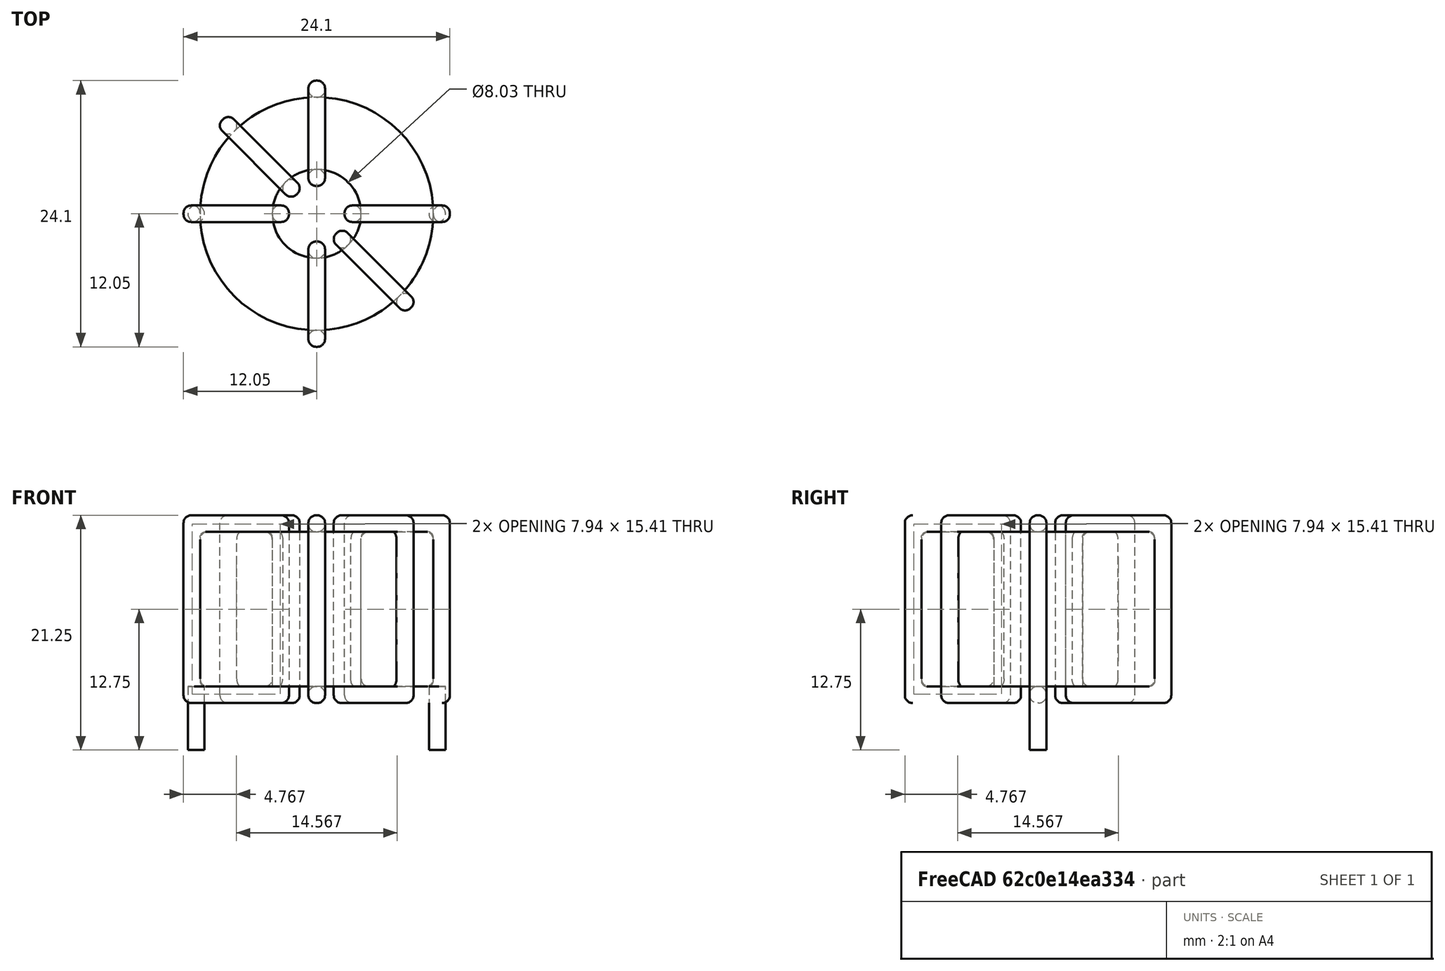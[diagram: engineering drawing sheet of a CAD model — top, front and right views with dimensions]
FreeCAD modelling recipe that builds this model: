
FCSTD DOCUMENT  (FreeCAD 0.16R6703 (Git))
Label: L_Toroid_Horizontal_D24.1mm_P21.80mm_Bourns_2200series
License: All rights reserved
LicenseURL: http://en.wikipedia.org/wiki/All_rights_reserved
objects: Sketcher::SketchObject×6, PartDesign::Pad×6, PartDesign::Fillet×5, Spreadsheet::Sheet×1
note: 23 computed .brp shape members not serialized (recipe doc carries the construction recipe); baked Part::Feature solids carry a one-line shape summary decoded from their .brp

FEATURE [Spreadsheet::Sheet] Spreadsheet  label="dimensions"
  cells = A1=Wx; B1(Wx)=24.1; C1(WW)=8.033333333333333; D1=24.1; A2=Wy; B2(Wy)=24.1; D2=24.1; A3=RM; B3(RMx)=21.8; C3(RMy)=0; A4=d_wire; B4(d_wire)=1.5; A5=H; B5(H)=14; A6=offsetx; B6(offsetx)=1.15
FEATURE [Sketcher::SketchObject] Sketch
  Placement = pos=(0,0,2) rot=(0,0,1;0rad)
  expr: Placement.Base.z = 0.5 + Spreadsheet.d_wire
  expr: Constraints[0] = Spreadsheet.Wx / 2 - Spreadsheet.d_wire
  expr: Constraints[4] = Spreadsheet.WW / 2
  expr: Constraints[2] = Spreadsheet.RMy / 2
  expr: Constraints[1] = Spreadsheet.RMx / 2
  sketch-geometry (2):
    g0: Circle CenterX=10.9 CenterY=0 CenterZ=0 NormalX=0 NormalY=0 NormalZ=1 Radius=10.55
    g1: Circle CenterX=10.9 CenterY=0 CenterZ=0 NormalX=0 NormalY=0 NormalZ=1 Radius=4.01667
  constraints (5):
    c: Radius(g0) = 10.55
    c: DistanceX(g-1,g0) = 10.9
    c: DistanceY(g-1,g0) = 0
    c: Coincident(g1,g0)
    c: Radius(g1) = 4.01667
FEATURE [PartDesign::Pad] Pad
  Length = 14
  Length2 = 100
  Placement = pos=(0,0,2) rot=(0,0,1;0rad)
  Sketch = -> Sketch
  Type = 0
  expr: Length = Spreadsheet.H
FEATURE [Sketcher::SketchObject] Sketch001
  Placement = pos=(0,0,1.25) rot=(0,0,1;0rad)
  expr: Placement.Base.z = 0.5 + Spreadsheet.d_wire * 0.5
  expr: Constraints[4] = Spreadsheet.RMx
  expr: Constraints[2] = Spreadsheet.RMy
  expr: Constraints[1] = Spreadsheet.d_wire / 2
  sketch-geometry (2):
    g0: Circle CenterX=0 CenterY=0 CenterZ=0 NormalX=0 NormalY=0 NormalZ=1 Radius=0.75
    g1: Circle CenterX=21.8 CenterY=0 CenterZ=0 NormalX=0 NormalY=0 NormalZ=1 Radius=0.75
  constraints (5):
    c: Equal(g0,g1)
    c: Radius(g0) = 0.75
    c: DistanceY(g-1,g1) = 0
    c: Coincident(g0,g-1)
    c: DistanceX(g-1,g1) = 21.8
FEATURE [PartDesign::Pad] Pad001
  Length = 0.75
  Length2 = 5
  Placement = pos=(0,0,1.25) rot=(0,0,1;0rad)
  Reversed = true
  Sketch = -> Sketch001
  Type = 4
  expr: Length2 = 3.5 + Spreadsheet.d_wire
  expr: Length = Spreadsheet.d_wire / 2
FEATURE [PartDesign::Fillet] Fillet
  Base = -> Pad [Edge6,Edge3,Edge2]
  Placement = pos=(0,0,2) rot=(0,0,1;0rad)
  Radius = 0.5
FEATURE [Sketcher::SketchObject] Sketch003
  Placement = pos=(10.9,0,0) rot=(1,0,0;1.5708rad)
  expr: Placement.Base.x = Spreadsheet.RMx / 2
  expr: Constraints[49] = Spreadsheet.Wx - Spreadsheet.d_wire * 2
  expr: Constraints[44] = Spreadsheet.d_wire
  expr: Constraints[23] = Spreadsheet.H
  expr: Constraints[22] = Spreadsheet.Wx / 2 - Spreadsheet.d_wire
  expr: Placement.Base.y = Spreadsheet.RMy / 2
  expr: Constraints[21] = (Spreadsheet.Wx - Spreadsheet.WW) / 2 - Spreadsheet.d_wire
  expr: Constraints[19] = Spreadsheet.d_wire
  expr: Constraints[17] = Spreadsheet.d_wire
  expr: Constraints[18] = Spreadsheet.d_wire
  expr: Constraints[16] = Spreadsheet.d_wire
  sketch-geometry (16):
    g0: LineSegment StartX=-2.51667 StartY=0.5 StartZ=0 EndX=-12.05 EndY=0.5 EndZ=0
    g1: LineSegment StartX=-12.05 StartY=0.5 StartZ=0 EndX=-12.05 EndY=17.5 EndZ=0
    g2: LineSegment StartX=-12.05 StartY=17.5 StartZ=0 EndX=-2.51667 EndY=17.5 EndZ=0
    g3: LineSegment StartX=-2.51667 StartY=17.5 StartZ=0 EndX=-2.51667 EndY=0.5 EndZ=0
    g4: LineSegment StartX=-10.55 StartY=16 StartZ=0 EndX=-4.01667 EndY=16 EndZ=0
    g5: LineSegment StartX=-4.01667 StartY=16 StartZ=0 EndX=-4.01667 EndY=2 EndZ=0
    g6: LineSegment StartX=-4.01667 StartY=2 StartZ=0 EndX=-10.55 EndY=2 EndZ=0
    g7: LineSegment StartX=-10.55 StartY=2 StartZ=0 EndX=-10.55 EndY=16 EndZ=0
    g8: LineSegment StartX=2.51667 StartY=17.5 StartZ=0 EndX=12.05 EndY=17.5 EndZ=0
    g9: LineSegment StartX=12.05 StartY=17.5 StartZ=0 EndX=12.05 EndY=0.5 EndZ=0
    g10: LineSegment StartX=12.05 StartY=0.5 StartZ=0 EndX=2.51667 EndY=0.5 EndZ=0
    g11: LineSegment StartX=2.51667 StartY=0.5 StartZ=0 EndX=2.51667 EndY=17.5 EndZ=0
    g12: LineSegment StartX=4.01667 StartY=16 StartZ=0 EndX=10.55 EndY=16 EndZ=0
    g13: LineSegment StartX=10.55 StartY=16 StartZ=0 EndX=10.55 EndY=2 EndZ=0
    g14: LineSegment StartX=10.55 StartY=2 StartZ=0 EndX=4.01667 EndY=2 EndZ=0
    g15: LineSegment StartX=4.01667 StartY=2 StartZ=0 EndX=4.01667 EndY=16 EndZ=0
  constraints (50):
    c: Horizontal(g0)
    c: Coincident(g1,g0)
    c: Vertical(g1)
    c: Coincident(g2,g1)
    c: Horizontal(g2)
    c: Coincident(g3,g2)
    c: Coincident(g3,g0)
    c: Vertical(g3)
    c: Coincident(g4,g5)
    c: Coincident(g5,g6)
    c: Coincident(g6,g7)
    c: Coincident(g7,g4)
    c: Horizontal(g4)
    c: Horizontal(g6)
    c: Vertical(g5)
    c: Vertical(g7)
    c: DistanceX(g1,g4) = 1.5
    c: DistanceY(g4,g1) = 1.5
    c: DistanceX(g5,g0) = 1.5
    c: DistanceY(g0,g5) = 1.5
    c: DistanceY(g-1,g0) = 0.5
    c: DistanceX(g6,g6) = 6.53333
    c: DistanceX(g6,g-1) = 10.55
    c: DistanceY(g7,g7) = 14
    c: Coincident(g8,g9)
    c: Coincident(g9,g10)
    c: Coincident(g10,g11)
    c: Coincident(g11,g8)
    c: Horizontal(g8)
    c: Horizontal(g10)
    c: Vertical(g9)
    c: Vertical(g11)
    c: Coincident(g12,g13)
    c: Coincident(g13,g14)
    c: Coincident(g14,g15)
    c: Coincident(g15,g12)
    c: Horizontal(g12)
    c: Horizontal(g14)
    c: Vertical(g13)
    c: Vertical(g15)
    c: DistanceY(g8,g2) = 0
    c: DistanceY(g10,g0) = 0
    c: DistanceY(g14,g5) = 0
    c: DistanceY(g12,g4) = 0
    c: DistanceX(g8,g12) = 1.5
    c: Equal(g8,g2)
    c: Equal(g12,g4)
    c: Equal(g9,g1)
    c: Equal(g13,g7)
    c: DistanceX(g4,g12) = 21.1
FEATURE [PartDesign::Pad] Pad002
  Length = 1.5
  Length2 = 100
  Midplane = true
  Placement = pos=(10.9,0,0) rot=(1,0,0;1.5708rad)
  Sketch = -> Sketch003
  Type = 0
  expr: Length = Spreadsheet.d_wire
FEATURE [PartDesign::Fillet] Fillet001
  Base = -> Pad002 [Edge38,Edge41,Edge42,Edge43,Edge29,Edge32,Edge33,Edge34,Edge25,Edge35,Edge36,Edge13,Edge14,Edge15,Edge16,Edge17,Edge18,Edge19,Edge1,Edge2,Edge3,Edge4,Edge5,Edge6,Edge7,Edge37,Edge39,Edge40,Edge20,Edge23,Edge24,Edge21,Edge22,Edge8,Edge9,Edge10,Edge11,Edge12,Edge26,Edge27,+8 more]
  Placement = pos=(10.9,0,0) rot=(1,0,0;1.5708rad)
  Radius = 0.705
  expr: Radius = Spreadsheet.d_wire * 0.47
FEATURE [Sketcher::SketchObject] Sketch004
  Placement = pos=(10.9,0,0) rot=(0.862856,0.357407,0.357407;1.71777rad)
  expr: Placement.Base.x = Spreadsheet.RMx / 2
  expr: Constraints[49] = Spreadsheet.Wx - 2 * Spreadsheet.d_wire
  expr: Constraints[44] = Spreadsheet.d_wire
  expr: Constraints[23] = Spreadsheet.H
  expr: Constraints[22] = Spreadsheet.Wx / 2 - Spreadsheet.d_wire
  expr: Placement.Base.y = Spreadsheet.RMy / 2
  expr: Constraints[21] = (Spreadsheet.Wx - Spreadsheet.WW) / 2 - Spreadsheet.d_wire
  expr: Constraints[19] = Spreadsheet.d_wire
  expr: Constraints[17] = Spreadsheet.d_wire
  expr: Constraints[18] = Spreadsheet.d_wire
  expr: Constraints[16] = Spreadsheet.d_wire
  sketch-geometry (16):
    g0: LineSegment StartX=-2.51667 StartY=0.5 StartZ=0 EndX=-12.05 EndY=0.5 EndZ=0
    g1: LineSegment StartX=-12.05 StartY=0.5 StartZ=0 EndX=-12.05 EndY=17.5 EndZ=0
    g2: LineSegment StartX=-12.05 StartY=17.5 StartZ=0 EndX=-2.51667 EndY=17.5 EndZ=0
    g3: LineSegment StartX=-2.51667 StartY=17.5 StartZ=0 EndX=-2.51667 EndY=0.5 EndZ=0
    g4: LineSegment StartX=-10.55 StartY=16 StartZ=0 EndX=-4.01667 EndY=16 EndZ=0
    g5: LineSegment StartX=-4.01667 StartY=16 StartZ=0 EndX=-4.01667 EndY=2 EndZ=0
    g6: LineSegment StartX=-4.01667 StartY=2 StartZ=0 EndX=-10.55 EndY=2 EndZ=0
    g7: LineSegment StartX=-10.55 StartY=2 StartZ=0 EndX=-10.55 EndY=16 EndZ=0
    g8: LineSegment StartX=2.51667 StartY=17.5 StartZ=0 EndX=12.05 EndY=17.5 EndZ=0
    g9: LineSegment StartX=12.05 StartY=17.5 StartZ=0 EndX=12.05 EndY=0.5 EndZ=0
    g10: LineSegment StartX=12.05 StartY=0.5 StartZ=0 EndX=2.51667 EndY=0.5 EndZ=0
    g11: LineSegment StartX=2.51667 StartY=0.5 StartZ=0 EndX=2.51667 EndY=17.5 EndZ=0
    g12: LineSegment StartX=4.01667 StartY=16 StartZ=0 EndX=10.55 EndY=16 EndZ=0
    g13: LineSegment StartX=10.55 StartY=16 StartZ=0 EndX=10.55 EndY=2 EndZ=0
    g14: LineSegment StartX=10.55 StartY=2 StartZ=0 EndX=4.01667 EndY=2 EndZ=0
    g15: LineSegment StartX=4.01667 StartY=2 StartZ=0 EndX=4.01667 EndY=16 EndZ=0
  constraints (50):
    c: Horizontal(g0)
    c: Coincident(g1,g0)
    c: Vertical(g1)
    c: Coincident(g2,g1)
    c: Horizontal(g2)
    c: Coincident(g3,g2)
    c: Coincident(g3,g0)
    c: Vertical(g3)
    c: Coincident(g4,g5)
    c: Coincident(g5,g6)
    c: Coincident(g6,g7)
    c: Coincident(g7,g4)
    c: Horizontal(g4)
    c: Horizontal(g6)
    c: Vertical(g5)
    c: Vertical(g7)
    c: DistanceX(g1,g4) = 1.5
    c: DistanceY(g4,g1) = 1.5
    c: DistanceX(g5,g0) = 1.5
    c: DistanceY(g0,g5) = 1.5
    c: DistanceY(g-1,g0) = 0.5
    c: DistanceX(g6,g6) = 6.53333
    c: DistanceX(g6,g-1) = 10.55
    c: DistanceY(g7,g7) = 14
    c: Coincident(g8,g9)
    c: Coincident(g9,g10)
    c: Coincident(g10,g11)
    c: Coincident(g11,g8)
    c: Horizontal(g8)
    c: Horizontal(g10)
    c: Vertical(g9)
    c: Vertical(g11)
    c: Coincident(g12,g13)
    c: Coincident(g13,g14)
    c: Coincident(g14,g15)
    c: Coincident(g15,g12)
    c: Horizontal(g12)
    c: Horizontal(g14)
    c: Vertical(g13)
    c: Vertical(g15)
    c: DistanceY(g8,g2) = 0
    c: DistanceY(g10,g0) = 0
    c: DistanceY(g14,g5) = 0
    c: DistanceY(g12,g4) = 0
    c: DistanceX(g8,g12) = 1.5
    c: Equal(g8,g2)
    c: Equal(g12,g4)
    c: Equal(g9,g1)
    c: Equal(g13,g7)
    c: DistanceX(g4,g12) = 21.1
FEATURE [PartDesign::Pad] Pad003
  Length = 1.5
  Length2 = 100
  Midplane = true
  Placement = pos=(10.9,0,0) rot=(0.862856,0.357407,0.357407;1.71777rad)
  Sketch = -> Sketch004
  Type = 0
  expr: Length = Spreadsheet.d_wire
FEATURE [PartDesign::Fillet] Fillet002
  Base = -> Pad003 [Edge38,Edge41,Edge42,Edge43,Edge29,Edge32,Edge33,Edge34,Edge25,Edge35,Edge36,Edge13,Edge14,Edge15,Edge16,Edge17,Edge18,Edge19,Edge1,Edge2,Edge3,Edge4,Edge5,Edge6,Edge7,Edge37,Edge39,Edge40,Edge20,Edge23,Edge24,Edge21,Edge22,Edge8,Edge9,Edge10,Edge11,Edge12,Edge26,Edge27,+8 more]
  Placement = pos=(10.9,0,0) rot=(0.862856,0.357407,0.357407;1.71777rad)
  Radius = 0.705
  expr: Radius = Spreadsheet.d_wire * 0.47
FEATURE [Sketcher::SketchObject] Sketch005
  Placement = pos=(10.9,0,0) rot=(0.862856,-0.357407,-0.357407;1.71777rad)
  expr: Placement.Base.x = Spreadsheet.RMx / 2
  expr: Constraints[49] = Spreadsheet.Wx - 2 * Spreadsheet.d_wire
  expr: Constraints[44] = Spreadsheet.d_wire
  expr: Constraints[23] = Spreadsheet.H
  expr: Constraints[22] = Spreadsheet.Wx / 2 - Spreadsheet.d_wire
  expr: Placement.Base.y = Spreadsheet.RMy / 2
  expr: Constraints[21] = (Spreadsheet.Wx - Spreadsheet.WW) / 2 - Spreadsheet.d_wire
  expr: Constraints[19] = Spreadsheet.d_wire
  expr: Constraints[17] = Spreadsheet.d_wire
  expr: Constraints[18] = Spreadsheet.d_wire
  expr: Constraints[16] = Spreadsheet.d_wire
  sketch-geometry (16):
    g0: LineSegment StartX=-2.51667 StartY=0.5 StartZ=0 EndX=-12.05 EndY=0.5 EndZ=0
    g1: LineSegment StartX=-12.05 StartY=0.5 StartZ=0 EndX=-12.05 EndY=17.5 EndZ=0
    g2: LineSegment StartX=-12.05 StartY=17.5 StartZ=0 EndX=-2.51667 EndY=17.5 EndZ=0
    g3: LineSegment StartX=-2.51667 StartY=17.5 StartZ=0 EndX=-2.51667 EndY=0.5 EndZ=0
    g4: LineSegment StartX=-10.55 StartY=16 StartZ=0 EndX=-4.01667 EndY=16 EndZ=0
    g5: LineSegment StartX=-4.01667 StartY=16 StartZ=0 EndX=-4.01667 EndY=2 EndZ=0
    g6: LineSegment StartX=-4.01667 StartY=2 StartZ=0 EndX=-10.55 EndY=2 EndZ=0
    g7: LineSegment StartX=-10.55 StartY=2 StartZ=0 EndX=-10.55 EndY=16 EndZ=0
    g8: LineSegment StartX=2.51667 StartY=17.5 StartZ=0 EndX=12.05 EndY=17.5 EndZ=0
    g9: LineSegment StartX=12.05 StartY=17.5 StartZ=0 EndX=12.05 EndY=0.5 EndZ=0
    g10: LineSegment StartX=12.05 StartY=0.5 StartZ=0 EndX=2.51667 EndY=0.5 EndZ=0
    g11: LineSegment StartX=2.51667 StartY=0.5 StartZ=0 EndX=2.51667 EndY=17.5 EndZ=0
    g12: LineSegment StartX=4.01667 StartY=16 StartZ=0 EndX=10.55 EndY=16 EndZ=0
    g13: LineSegment StartX=10.55 StartY=16 StartZ=0 EndX=10.55 EndY=2 EndZ=0
    g14: LineSegment StartX=10.55 StartY=2 StartZ=0 EndX=4.01667 EndY=2 EndZ=0
    g15: LineSegment StartX=4.01667 StartY=2 StartZ=0 EndX=4.01667 EndY=16 EndZ=0
  constraints (50):
    c: Horizontal(g0)
    c: Coincident(g1,g0)
    c: Vertical(g1)
    c: Coincident(g2,g1)
    c: Horizontal(g2)
    c: Coincident(g3,g2)
    c: Coincident(g3,g0)
    c: Vertical(g3)
    c: Coincident(g4,g5)
    c: Coincident(g5,g6)
    c: Coincident(g6,g7)
    c: Coincident(g7,g4)
    c: Horizontal(g4)
    c: Horizontal(g6)
    c: Vertical(g5)
    c: Vertical(g7)
    c: DistanceX(g1,g4) = 1.5
    c: DistanceY(g4,g1) = 1.5
    c: DistanceX(g5,g0) = 1.5
    c: DistanceY(g0,g5) = 1.5
    c: DistanceY(g-1,g0) = 0.5
    c: DistanceX(g6,g6) = 6.53333
    c: DistanceX(g6,g-1) = 10.55
    c: DistanceY(g7,g7) = 14
    c: Coincident(g8,g9)
    c: Coincident(g9,g10)
    c: Coincident(g10,g11)
    c: Coincident(g11,g8)
    c: Horizontal(g8)
    c: Horizontal(g10)
    c: Vertical(g9)
    c: Vertical(g11)
    c: Coincident(g12,g13)
    c: Coincident(g13,g14)
    c: Coincident(g14,g15)
    c: Coincident(g15,g12)
    c: Horizontal(g12)
    c: Horizontal(g14)
    c: Vertical(g13)
    c: Vertical(g15)
    c: DistanceY(g8,g2) = 0
    c: DistanceY(g10,g0) = 0
    c: DistanceY(g14,g5) = 0
    c: DistanceY(g12,g4) = 0
    c: DistanceX(g8,g12) = 1.5
    c: Equal(g8,g2)
    c: Equal(g12,g4)
    c: Equal(g9,g1)
    c: Equal(g13,g7)
    c: DistanceX(g4,g12) = 21.1
FEATURE [PartDesign::Pad] Pad004
  Length = 1.5
  Length2 = 100
  Midplane = true
  Placement = pos=(10.9,0,0) rot=(0.862856,-0.357407,-0.357407;1.71777rad)
  Sketch = -> Sketch005
  Type = 0
  expr: Length = Spreadsheet.d_wire
FEATURE [PartDesign::Fillet] Fillet003
  Base = -> Pad004 [Edge38,Edge41,Edge42,Edge43,Edge29,Edge32,Edge33,Edge34,Edge25,Edge35,Edge36,Edge13,Edge14,Edge15,Edge16,Edge17,Edge18,Edge19,Edge1,Edge2,Edge3,Edge4,Edge5,Edge6,Edge7,Edge37,Edge39,Edge40,Edge20,Edge23,Edge24,Edge21,Edge22,Edge8,Edge9,Edge10,Edge11,Edge12,Edge26,Edge27,+8 more]
  Placement = pos=(10.9,0,0) rot=(0.862856,-0.357407,-0.357407;1.71777rad)
  Radius = 0.705
  expr: Radius = Spreadsheet.d_wire * 0.47
FEATURE [Sketcher::SketchObject] Sketch006
  Placement = pos=(10.9,0,0) rot=(0.57735,0.57735,0.57735;2.0944rad)
  expr: Placement.Base.x = Spreadsheet.RMx / 2
  expr: Constraints[49] = Spreadsheet.Wx - Spreadsheet.d_wire * 2
  expr: Constraints[44] = Spreadsheet.d_wire
  expr: Constraints[23] = Spreadsheet.H
  expr: Constraints[22] = Spreadsheet.Wx / 2 - Spreadsheet.d_wire
  expr: Placement.Base.y = Spreadsheet.RMy / 2
  expr: Constraints[21] = (Spreadsheet.Wx - Spreadsheet.WW) / 2 - Spreadsheet.d_wire
  expr: Constraints[19] = Spreadsheet.d_wire
  expr: Constraints[17] = Spreadsheet.d_wire
  expr: Constraints[18] = Spreadsheet.d_wire
  expr: Constraints[16] = Spreadsheet.d_wire
  sketch-geometry (16):
    g0: LineSegment StartX=-2.51667 StartY=0.5 StartZ=0 EndX=-12.05 EndY=0.5 EndZ=0
    g1: LineSegment StartX=-12.05 StartY=0.5 StartZ=0 EndX=-12.05 EndY=17.5 EndZ=0
    g2: LineSegment StartX=-12.05 StartY=17.5 StartZ=0 EndX=-2.51667 EndY=17.5 EndZ=0
    g3: LineSegment StartX=-2.51667 StartY=17.5 StartZ=0 EndX=-2.51667 EndY=0.5 EndZ=0
    g4: LineSegment StartX=-10.55 StartY=16 StartZ=0 EndX=-4.01667 EndY=16 EndZ=0
    g5: LineSegment StartX=-4.01667 StartY=16 StartZ=0 EndX=-4.01667 EndY=2 EndZ=0
    g6: LineSegment StartX=-4.01667 StartY=2 StartZ=0 EndX=-10.55 EndY=2 EndZ=0
    g7: LineSegment StartX=-10.55 StartY=2 StartZ=0 EndX=-10.55 EndY=16 EndZ=0
    g8: LineSegment StartX=2.51667 StartY=17.5 StartZ=0 EndX=12.05 EndY=17.5 EndZ=0
    g9: LineSegment StartX=12.05 StartY=17.5 StartZ=0 EndX=12.05 EndY=0.5 EndZ=0
    g10: LineSegment StartX=12.05 StartY=0.5 StartZ=0 EndX=2.51667 EndY=0.5 EndZ=0
    g11: LineSegment StartX=2.51667 StartY=0.5 StartZ=0 EndX=2.51667 EndY=17.5 EndZ=0
    g12: LineSegment StartX=4.01667 StartY=16 StartZ=0 EndX=10.55 EndY=16 EndZ=0
    g13: LineSegment StartX=10.55 StartY=16 StartZ=0 EndX=10.55 EndY=2 EndZ=0
    g14: LineSegment StartX=10.55 StartY=2 StartZ=0 EndX=4.01667 EndY=2 EndZ=0
    g15: LineSegment StartX=4.01667 StartY=2 StartZ=0 EndX=4.01667 EndY=16 EndZ=0
  constraints (50):
    c: Horizontal(g0)
    c: Coincident(g1,g0)
    c: Vertical(g1)
    c: Coincident(g2,g1)
    c: Horizontal(g2)
    c: Coincident(g3,g2)
    c: Coincident(g3,g0)
    c: Vertical(g3)
    c: Coincident(g4,g5)
    c: Coincident(g5,g6)
    c: Coincident(g6,g7)
    c: Coincident(g7,g4)
    c: Horizontal(g4)
    c: Horizontal(g6)
    c: Vertical(g5)
    c: Vertical(g7)
    c: DistanceX(g1,g4) = 1.5
    c: DistanceY(g4,g1) = 1.5
    c: DistanceX(g5,g0) = 1.5
    c: DistanceY(g0,g5) = 1.5
    c: DistanceY(g-1,g0) = 0.5
    c: DistanceX(g6,g6) = 6.53333
    c: DistanceX(g6,g-1) = 10.55
    c: DistanceY(g7,g7) = 14
    c: Coincident(g8,g9)
    c: Coincident(g9,g10)
    c: Coincident(g10,g11)
    c: Coincident(g11,g8)
    c: Horizontal(g8)
    c: Horizontal(g10)
    c: Vertical(g9)
    c: Vertical(g11)
    c: Coincident(g12,g13)
    c: Coincident(g13,g14)
    c: Coincident(g14,g15)
    c: Coincident(g15,g12)
    c: Horizontal(g12)
    c: Horizontal(g14)
    c: Vertical(g13)
    c: Vertical(g15)
    c: DistanceY(g8,g2) = 0
    c: DistanceY(g10,g0) = 0
    c: DistanceY(g14,g5) = 0
    c: DistanceY(g12,g4) = 0
    c: DistanceX(g8,g12) = 1.5
    c: Equal(g8,g2)
    c: Equal(g12,g4)
    c: Equal(g9,g1)
    c: Equal(g13,g7)
    c: DistanceX(g4,g12) = 21.1
FEATURE [PartDesign::Pad] Pad005
  Length = 1.5
  Length2 = 100
  Midplane = true
  Placement = pos=(10.9,0,0) rot=(0.57735,0.57735,0.57735;2.0944rad)
  Sketch = -> Sketch006
  Type = 0
  expr: Length = Spreadsheet.d_wire
FEATURE [PartDesign::Fillet] Fillet004
  Base = -> Pad005 [Edge38,Edge41,Edge42,Edge43,Edge29,Edge32,Edge33,Edge34,Edge25,Edge35,Edge36,Edge13,Edge14,Edge15,Edge16,Edge17,Edge18,Edge19,Edge1,Edge2,Edge3,Edge4,Edge5,Edge6,Edge7,Edge37,Edge39,Edge40,Edge20,Edge23,Edge24,Edge21,Edge22,Edge8,Edge9,Edge10,Edge11,Edge12,Edge26,Edge27,+8 more]
  Placement = pos=(10.9,0,0) rot=(0.57735,0.57735,0.57735;2.0944rad)
  Radius = 0.705
  expr: Radius = Spreadsheet.d_wire * 0.47
